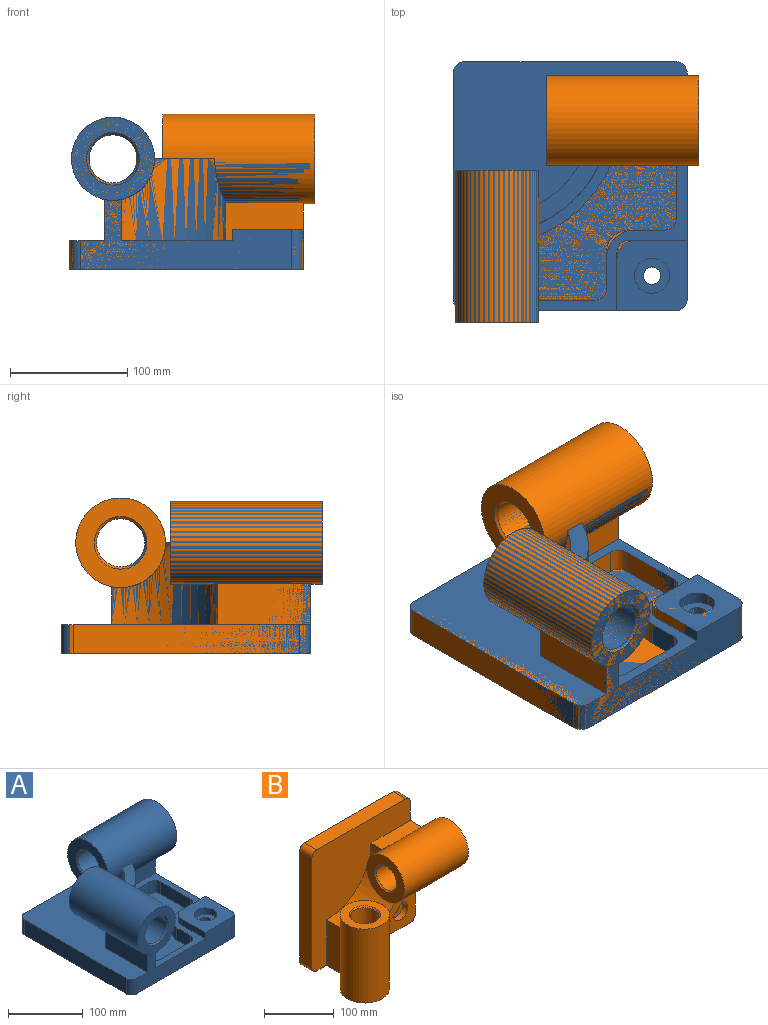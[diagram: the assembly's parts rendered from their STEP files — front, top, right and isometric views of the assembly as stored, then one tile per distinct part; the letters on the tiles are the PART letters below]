
ASSEMBLY  parts=2 mates=1
PART A: 52 faces, bbox 210x223x133.3 mm
  f0: cylinder r=105mm len=88.92mm, axis (0,0,-1), area 7781mm2, adj f2,f3,f5,f7,f27,f31
  f1: cylinder r=90mm len=90mm, axis (0,0,-1), area 7108.5mm2, adj f2,f4,f6,f20,f27,f31
  f2: plane 51.47x49.96mm, normal (0,0,1), area 913.2mm2, adj f0,f1,f27,f31
  f3: plane 66.08x32.41mm, normal (0,-1,0), area 2141.4mm2, adj f0,f7,f15,f31
  f4: plane 80x32.41mm, normal (0,1,0), area 2592.6mm2, adj f1,f15,f20,f31
  f5: plane 66.08x35.3mm, normal (1,0,0), area 2332.6mm2, adj f0,f7,f18,f27
  f6: plane 80x35.3mm, normal (-1,0,0), area 2824.1mm2, adj f1,f18,f20,f27
  f7: plane 155x155mm, normal (0,0,1), area 4896.4mm2, adj f0,f3,f5,f8,f9,f10,f11,f12
  f8: plane 26x20mm, normal (-1,0,0), area 520mm2, adj f7,f19,f22,f42
  f9: plane 57x20mm, normal (0,1,0), area 1140mm2, adj f7,f22,f42,f43
  f10: plane 31.75x20mm, normal (1,0,0), area 635mm2, adj f7,f22,f43,f44
  f11: cylinder r=114mm len=78.37mm, axis (0,0,-1), area 2314.9mm2, adj f7,f22,f44,f45
  f12: plane 31.75x20mm, normal (0,-1,0), area 635mm2, adj f7,f22,f45,f46
  f13: plane 57x20mm, normal (-1,0,0), area 1140mm2, adj f7,f22,f46,f47
  f14: plane 26x20mm, normal (0,1,0), area 520mm2, adj f7,f19,f22,f47
  f15: plane 193x57.41mm, normal (1,0,0), area 5803.7mm2, adj f3,f4,f7,f20,f21,f23,f26,f31
  f16: plane 180x25mm, normal (0,1,0), area 4500mm2, adj f20,f21,f39,f40
  f17: plane 193x25mm, normal (-1,0,0), area 4825mm2, adj f20,f21,f40,f41
  f18: plane 180x60.3mm, normal (0,-1,0), area 5521.5mm2, adj f5,f6,f7,f20,f21,f25,f26,f27
  f19: cylinder r=24mm len=24mm, axis (0,0,-1), area 754mm2, adj f7,f8,f14,f22
  f20: plane 213x200mm, normal (0,0,1), area 19997.3mm2, adj f1,f4,f6,f15,f16,f17,f18,f39
  f21: plane 213x200mm, normal (0,0,-1), area 42337.4mm2, adj f15,f16,f17,f18,f35,f38,f39,f40
  f22: plane 137x137mm, normal (0,0,1), area 9832.2mm2, adj f8,f9,f10,f11,f12,f13,f14,f19
  f23: plane 45x10mm, normal (0,1,0), area 450mm2, adj f7,f15,f24,f26
  f24: cylinder r=15mm len=15mm, axis (0,0,-1), area 235.6mm2, adj f7,f23,f25,f26
  f25: plane 45x10mm, normal (-1,0,0), area 450mm2, adj f7,f18,f24,f26
  f26: plane 60x60mm, normal (0,0,1), area 2823.4mm2, adj f15,f18,f23,f24,f25,f37,f38
  f27: cylinder r=35.5mm len=130mm, axis (0,1,0), area 27007.9mm2, adj f0,f1,f2,f5,f6,f18,f29,f30
  f28: cylinder r=20.5mm len=126mm, axis (0,1,0), area 16229.5mm2, adj f48,f49
  f29: plane 71x71mm, normal (0,-1,0), area 2368.8mm2, adj f27,f48
  f30: plane 71x71mm, normal (0,1,0), area 2368.8mm2, adj f27,f49
  f31: cylinder r=38.33mm len=130mm, axis (-1,0,0), area 29244.3mm2, adj f0,f1,f2,f3,f4,f15,f33,f34
  f32: cylinder r=20.5mm len=126mm, axis (-1,0,0), area 16229.5mm2, adj f50,f51
  f33: plane 76.67x76.67mm, normal (1,0,0), area 3026mm2, adj f31,f50
  f34: plane 76.67x76.67mm, normal (-1,0,0), area 3026mm2, adj f31,f51
  f35: cylinder r=7.5mm len=25mm, axis (0,0,1), area 1178.1mm2, adj f21,f36
  f36: plane 30x30mm, normal (0,0,1), area 530.1mm2, adj f35,f37
  f37: cylinder r=15mm len=30mm, axis (0,0,1), area 942.5mm2, adj f26,f36
  f38: cylinder r=10mm len=35mm, axis (0,0,1), area 549.8mm2, adj f15,f18,f21,f26
  f39: cylinder r=10mm len=25mm, axis (0,0,-1), area 392.7mm2, adj f15,f16,f20,f21
  f40: cylinder r=10mm len=25mm, axis (0,0,1), area 392.7mm2, adj f16,f17,f20,f21
  f41: cylinder r=10mm len=25mm, axis (0,0,-1), area 392.7mm2, adj f17,f18,f20,f21
  f42: cylinder r=10mm len=20mm, axis (0,0,1), area 314.2mm2, adj f7,f8,f9,f22
  f43: cylinder r=10mm len=20mm, axis (0,0,-1), area 314.2mm2, adj f7,f9,f10,f22
  f44: cylinder r=10mm len=20mm, axis (0,0,-1), area 258.6mm2, adj f7,f10,f11,f22
  f45: cylinder r=10mm len=20mm, axis (0,0,-1), area 258.6mm2, adj f7,f11,f12,f22
  f46: cylinder r=10mm len=20mm, axis (0,0,-1), area 314.2mm2, adj f7,f12,f13,f22
  f47: cylinder r=10mm len=20mm, axis (0,0,1), area 314.2mm2, adj f7,f13,f14,f22
  f48: cone r=20.5mm half-angle=45deg, axis (0,-1,0), area 382.1mm2, adj f28,f29
  f49: cone r=22.5mm half-angle=45deg, axis (0,1,0), area 382.1mm2, adj f28,f30
  f50: cone r=20.5mm half-angle=45deg, axis (1,0,0), area 382.1mm2, adj f32,f33
  f51: cone r=22.5mm half-angle=45deg, axis (-1,0,0), area 382.1mm2, adj f32,f34
PART B: 52 faces, bbox 210x133.3x223 mm
  f0: plane 155x155mm, normal (0,-1,0), area 4915.7mm2, adj f3,f4,f7,f8,f9,f22,f23,f25
  f1: plane 213x200mm, normal (0,-1,0), area 19997.3mm2, adj f2,f3,f4,f5,f10,f11,f12,f44
  f2: plane 193x25mm, normal (-1,0,0), area 4825mm2, adj f1,f6,f45,f46
  f3: plane 180x60.3mm, normal (0,0,-1), area 5521.5mm2, adj f0,f1,f6,f7,f12,f14,f23,f24
  f4: plane 193x57.41mm, normal (1,0,0), area 5803.7mm2, adj f0,f1,f6,f9,f10,f17,f22,f24
  f5: plane 180x25mm, normal (0,0,1), area 4500mm2, adj f1,f6,f44,f45
  f6: plane 213x200mm, normal (0,1,0), area 42337.4mm2, adj f2,f3,f4,f5,f41,f44,f45,f46
  f7: plane 66.08x35.3mm, normal (1,0,0), area 2332.6mm2, adj f0,f3,f8,f14
  f8: cylinder r=105mm len=88.92mm, axis (0,1,0), area 7780.9mm2, adj f0,f7,f9,f13,f14,f17
  f9: plane 66.08x32.41mm, normal (0,0,-1), area 2141.3mm2, adj f0,f4,f8,f17
  f10: plane 80x32.41mm, normal (0,0,1), area 2592.5mm2, adj f1,f4,f11,f17
  f11: cylinder r=90mm len=90mm, axis (0,1,0), area 7108.2mm2, adj f1,f10,f12,f13,f14,f17
  f12: plane 80x35.3mm, normal (-1,0,0), area 2824.1mm2, adj f1,f3,f11,f14
  f13: plane 51.47x49.96mm, normal (0,-1,0), area 913.2mm2, adj f8,f11,f14,f17
  f14: cylinder r=35.5mm len=130mm, axis (0,0,-1), area 27007.9mm2, adj f3,f7,f8,f11,f12,f13,f15,f16
  f15: plane 71x71mm, normal (0,0,1), area 2368.8mm2, adj f14,f50
  f16: plane 71x71mm, normal (0,0,-1), area 2368.8mm2, adj f14,f51
  f17: cylinder r=38.34mm len=130mm, axis (1,0,0), area 29245.6mm2, adj f4,f8,f9,f10,f11,f13,f18,f19
  f18: plane 76.67x76.67mm, normal (-1,0,0), area 3026.4mm2, adj f17,f49
  f19: plane 76.67x76.67mm, normal (1,0,0), area 3026.4mm2, adj f17,f48
  f20: cylinder r=20.5mm len=126mm, axis (0,0,-1), area 16229.5mm2, adj f50,f51
  f21: cylinder r=20.5mm len=126mm, axis (1,0,0), area 16229.5mm2, adj f48,f49
  f22: plane 50x10mm, normal (0,0,1), area 500mm2, adj f0,f4,f24,f25
  f23: plane 50x10mm, normal (-1,0,0), area 500mm2, adj f0,f3,f24,f25
  f24: plane 60x60mm, normal (0,-1,0), area 2850.2mm2, adj f3,f4,f22,f23,f25,f43,f47
  f25: cylinder r=10mm len=10mm, axis (0,1,0), area 157.1mm2, adj f0,f22,f23,f24
  f26: cylinder r=10mm len=20mm, axis (0,-1,0), area 258.6mm2, adj f0,f27,f39,f40
  f27: plane 31.75x20mm, normal (0,0,-1), area 635mm2, adj f0,f26,f28,f40
  f28: cylinder r=10mm len=20mm, axis (0,-1,0), area 314.2mm2, adj f0,f27,f29,f40
  f29: plane 57x20mm, normal (-1,0,0), area 1140mm2, adj f0,f28,f30,f40
  f30: cylinder r=10mm len=20mm, axis (0,-1,0), area 314.2mm2, adj f0,f29,f31,f40
  f31: plane 31x20mm, normal (0,0,1), area 620mm2, adj f0,f30,f32,f40
  f32: cylinder r=19mm len=20mm, axis (0,-1,0), area 596.9mm2, adj f0,f31,f33,f40
  f33: plane 31x20mm, normal (-1,0,0), area 620mm2, adj f0,f32,f34,f40
  f34: cylinder r=10mm len=20mm, axis (0,-1,0), area 314.2mm2, adj f0,f33,f35,f40
  f35: plane 57x20mm, normal (0,0,1), area 1140mm2, adj f0,f34,f36,f40
  f36: cylinder r=10mm len=20mm, axis (0,-1,0), area 314.2mm2, adj f0,f35,f37,f40
  f37: plane 31.75x20mm, normal (1,0,0), area 635mm2, adj f0,f36,f38,f40
  f38: cylinder r=10mm len=20mm, axis (0,-1,0), area 258.6mm2, adj f0,f37,f39,f40
  f39: cylinder r=114mm len=78.37mm, axis (0,-1,0), area 2314.9mm2, adj f0,f26,f38,f40
  f40: plane 137x137mm, normal (0,-1,0), area 9786mm2, adj f26,f27,f28,f29,f30,f31,f32,f33
  f41: cylinder r=7.5mm len=25mm, axis (0,-1,0), area 1178.1mm2, adj f6,f42
  f42: plane 30x30mm, normal (0,-1,0), area 530.1mm2, adj f41,f43
  f43: cylinder r=15mm len=30mm, axis (0,-1,0), area 942.5mm2, adj f24,f42
  f44: cylinder r=10mm len=25mm, axis (0,1,0), area 392.7mm2, adj f1,f4,f5,f6
  f45: cylinder r=10mm len=25mm, axis (0,1,0), area 392.7mm2, adj f1,f2,f5,f6
  f46: cylinder r=10mm len=25mm, axis (0,1,0), area 392.7mm2, adj f1,f2,f3,f6
  f47: cylinder r=10mm len=35mm, axis (0,1,0), area 549.8mm2, adj f3,f4,f6,f24
  f48: cone r=20.5mm half-angle=45deg, axis (1,0,0), area 382.1mm2, adj f19,f21
  f49: cone r=22.5mm half-angle=45deg, axis (-1,0,0), area 382.1mm2, adj f18,f21
  f50: cone r=22.5mm half-angle=45deg, axis (0,0,1), area 382.1mm2, adj f15,f20
  f51: cone r=20.5mm half-angle=45deg, axis (0,0,-1), area 382.1mm2, adj f16,f20
PLACE A t=(-107.36,-84.95,3.02)mm
PLACE B rot(axis=(-1,0,0),90deg) t=(-207.36,21.55,3.02)mm
MATE planar B.f2 <-> A.f17  axis (-1,0,0) through (-307.36,21.55,15.52)mm
